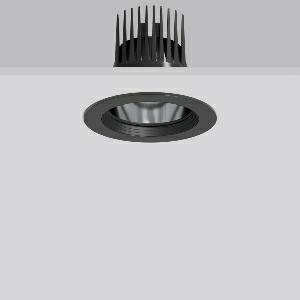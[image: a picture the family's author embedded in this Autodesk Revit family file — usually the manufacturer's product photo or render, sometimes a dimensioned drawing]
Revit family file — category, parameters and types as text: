
# Revit family: heledon_maxi_e_901764_003_1_29dd
name_source: partatom
category: Lighting Fixtures
units: mm (PartAtom-declared; Revit-internal decimal feet)

## family parameters
Cut with Voids When Loaded = No
Host = Face
Light Source = No
Part Type = Normal
Room Calculation Point = No
Round Connector Dimension = Use Diameter
Shared = No

## types (1)
- HELEDON maxi E (1 x LED Modul 940, 4550 lm, 4000)
    Apparent Load = 35 VA
    Approval mark = CE
    CIE Flux Codes = 100 100 100 100 100
    Color Rendering = 92
    Color Temperature = 4000
    Default Elevation = 1800 mm
    Description = Series: HELEDON maxi
Round recessed downlight. Housing: die-cast aluminium, powder-coated. Black plastic ring and recessed LED to prevent glare from the side. Optical assembly with reflector made of MIRO-Silver with 98% total light reflection for outstanding efficiency - can be changed without tools. Best colour rendering index Ra>90. Suitable for Recessed ceiling mounting. Installation without tools thanks to spring fastening system. Including separate LED converter with connecting cable 600 mm.High quality converter without flickering and stroboscopic effect. Through-wiring box (5 pole) available as accessory. The following accessories can be mounted without use of tools: interchangeable lenses, decorative glasses, honeycomb louvre, clear and frosted diffusers, white interchangeable plastic ring. 
Colour: deep black, matt (RAL 9005)
Diameter: 162 mm
Height: 3 mm
Cut-out diameter: 152 mm
Recess height: 200 mm
Luminaire: recess height: 135 mm
Lamp: LED
Socket: without socket
Colour temperature: 4000K
Colour rendering index (CRI): 92
System power: 35 W
Rated luminous flux: 4550 lm
Luminous efficiency: 130 lm/W
Control gear: Regulated power supply
Protection class: II
Type of protection: IP 20
    Height = 0 mm  [stored 0 ft]
    Lamp = 1 x LED Modul 940
    Lamp Light Flux = 4550 lm
    Lamp count = 1
    Length = 162 mm
    Lifetime = 50000 h
    Luminous efficacy = 130 lm/W
    Manufacturer = RZB
    ModVariant = No
    Model = 901764.003.1
    Mounting Place = Ceiling
    Mounting Type = Recessed
    Number of Poles = 1
    OnlyDefault = Yes
    Power Factor = 1
    Product Name = HELEDON maxi E
    Product group = Recessed downlights
    ProductGroupID = 402
    Protection Class = Protection class II
    Protection Degree = IP 20
    RLX_Detail_Level = 1
    RLX_Emergency_Light_Flux = 0 lm
    RLX_Emergency_Type = 0
    RLX_Emergency_Type_DB = No
    RlxData = <blob elided: 120225 chars, md5=2df5f2c1>
    Socket = socket
    Standby Power = 0 W
    System Light Flux = 4550 lm
    System Power = 35 W
    Type Comments = Product without accessories
    Type Image = 901662.003.jpg
    URL = http://relux.com
    VarID = ---
    Voltage = 230 V
    Voltage Range = 220-240 V
    Weight = 0.00 kg
    Width = 0 mm  [stored 0 ft]

note: [stored X ft] marks values corroborated as IEEE doubles in the binary element streams (Revit-internal decimal feet)

## geometry (parser evidence)
native form markers: Blend x4, Sweep x12
no freeform markers — native parametric forms only
